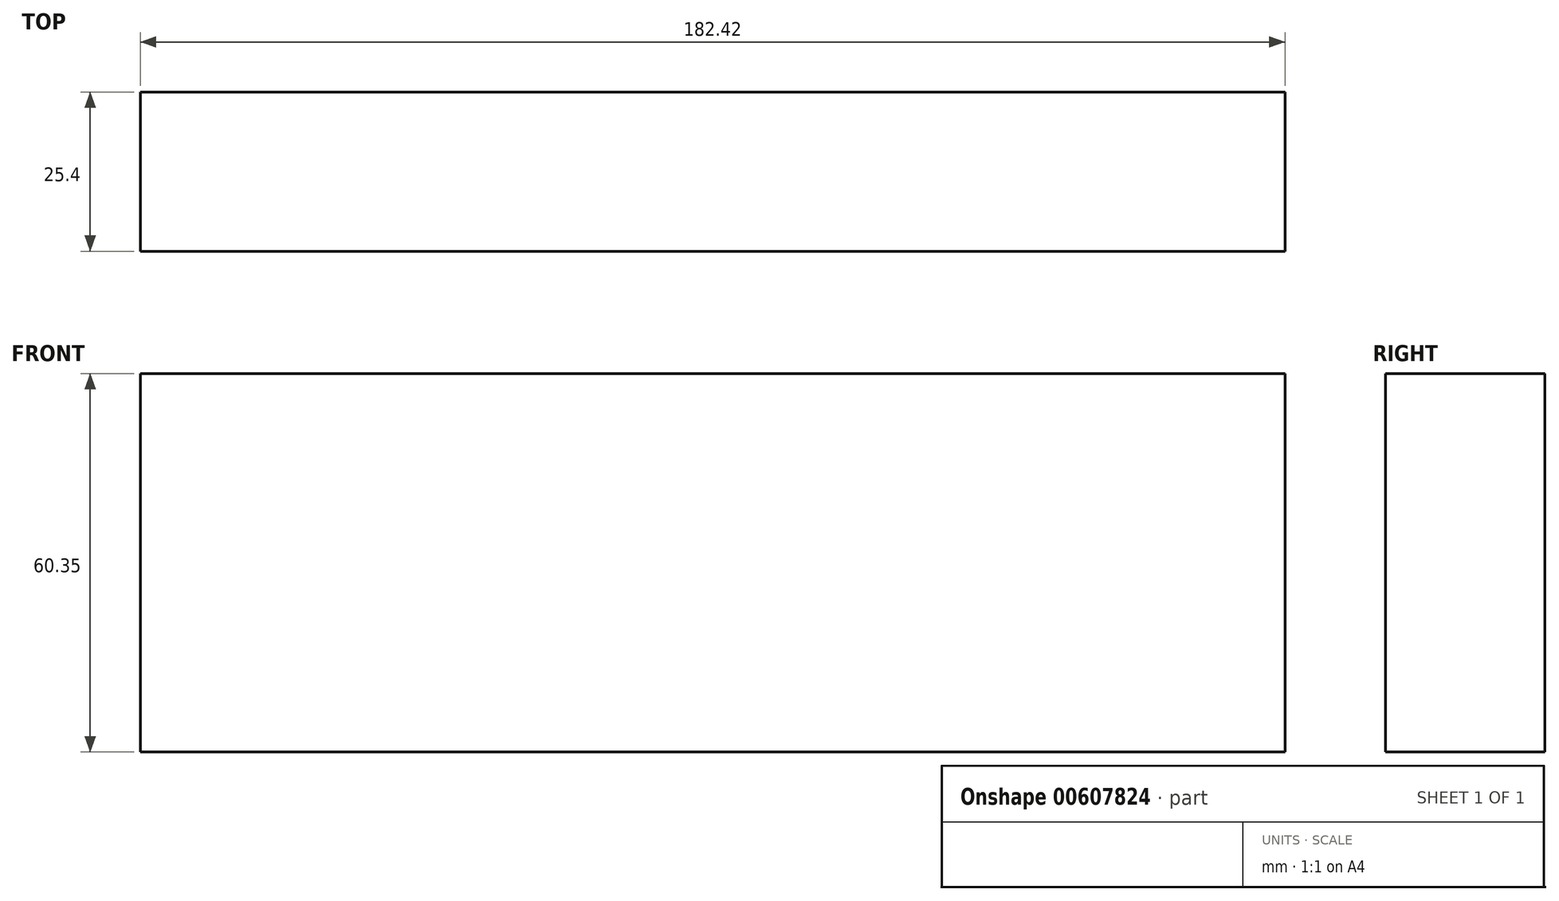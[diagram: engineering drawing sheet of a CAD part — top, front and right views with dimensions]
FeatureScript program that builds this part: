
annotation { "Feature Type Name" : "Feature", "Feature Type Description" : "" }
export const myFeature = defineFeature(function(context is Context, id is Id, definition is map)
    precondition{}
    {
        {
            var Q0;
            Q0=qCreatedBy(makeId("Front.planeOp"),FACE);
            var sketch = newSketch(context, id + "F0", { "sketchPlane" : qUnion([Q0])});
            skLineSegment(sketch, "E0.bottom", {"start": v(91.2, 50.02) * mm, "end": v(-91.2, 50.02) * mm});
            skLineSegment(sketch, "E0.top", {"start": v(91.2, -10.33) * mm, "end": v(-91.2, -10.33) * mm});
            skLineSegment(sketch, "E0.left", {"start": v(91.2, 50.02) * mm, "end": v(91.2, -10.33) * mm});
            skLineSegment(sketch, "E0.right", {"start": v(-91.2, 50.02) * mm, "end": v(-91.2, -10.33) * mm});
            skPoint(sketch, "E0.middle", {"position": v(0, 19.84) * mm});
            skSolve(sketch);
        }
        {
            var Q0;
            Q0 = qSketchRegion(id + "F0", true);
            extrude(context, id + "F1", {"entities" : qUnion([Q0]), "depth" : 25.4 * mm, "offsetDistance" : 25.4 * mm});
        }
    });
